# Revit family: VLGFS1502-xxxWS8xxBQPxxxx
name_source: partatom
category: Oprawy oświetleniowe
revit_build: Autodesk Revit 2017 (Build: 20190507_1515(x64)
units: mm (PartAtom-declared; Revit-internal decimal feet)

## family parameters
Numer OmniClass = 23.80.70.11
Obiekt nadrzędny = Powierzchnia
Punkt obliczania pomieszczeń = Nie
Tnij formami wycięć po wczytaniu = Nie
Typ części = Normalny
Tytuł OmniClass = Luminaries for Internal Lighting
Współdzielony = Nie
Wymiar okrągłego złącza = Użyj średnicy
Źródło światła = Tak

## types (16) — shared parameters
Emituj kształt widoczny w renderingu = Nie
Emituj z długości prostokąta = 94 mm  [stored 0.308399 ft]
Emituj z szerokości prostokąta = 1477 mm  [stored 4.8458 ft]
Filtr koloru = 16777215
Kod zespołu = D5020200
Lampa = LED
Odchylenie kierunku = 90.00°
Plik sieci fotometrycznej = VLGFS1502-5NDWS840BQP1500.IES
Producent = RIDI Leuchten GmbH
URL = www.ridi.de
Zmiana temperatury barwowej przyciemniania lampy = <Brak>
brand = RIDI
conformity mark = CE
electrical safety class = 1
height = 74 mm  [stored 0.242782 ft]
ingress protection (IP) code = IP54
length = 1500 mm  [stored 4.92126 ft]
nominal frequency = 50-60Hz
nominal voltage = 230
voltage type (AC, DC, UC) = AC
weight = 3.019 kg
width = 97 mm  [stored 0.318241 ft]
zero-valued in all types: Domyślna rzędna

## per-type parameters (varying)
| type | Model | Obciążenie pozorne | rated input power |
| VLGFS1502-5NDWS830BQP0750 | 1551302 | 60 VA | 60 |
| VLGFS1502-7DAWS830BQP0750 | 1561302 | 60 VA | 60 |
| VLGFS1502-5NDWS830BQP1500 | 1551238 | 117 VA | 117 |
| VLGFS1502-7DAWS830BQP1500 | 1561238 | 117 VA | 117 |
| VLGFS1502-7DAWS840BQP0750 | 1561306 | 60 VA | 60 |
| VLGFS1502-5NDWS840BQP1500 | 1551235 | 117 VA | 117 |
| VLGFS1502-7DAWS840BQP1500 | 1561235 | 117 VA | 117 |
| VLGFS1502-5NDWS850BQP0800 | 1551308 | 60 VA | 60 |
| VLGFS1502-7DAWS850BQP0800 | 1561308 | 60 VA | 60 |
| VLGFS1502-5NDWS850BQP1500 | 1551241 | 117 VA | 117 |
| VLGFS1502-7DAWS850BQP1500 | 1561241 | 117 VA | 117 |
| VLGFS1502-5NDWS865BQP0750 | 1551311 | 60 VA | 60 |
| VLGFS1502-5NDWS865BQP1500 | 1551244 | 117 VA | 117 |
| VLGFS1502-5NDWS840BQP0750 | 1551306 | 60 VA | 60 |
| VLGFS1502-7DAWS865BQP0750 | 1561311 | 60 VA | 60 |
| VLGFS1502-7DAWS865BQP1500 | 1561244 | 117 VA | 117 |

note: column(s) folded — value = type name in every type: product name

note: [stored X ft] marks values corroborated as IEEE doubles in the binary element streams (Revit-internal decimal feet)
